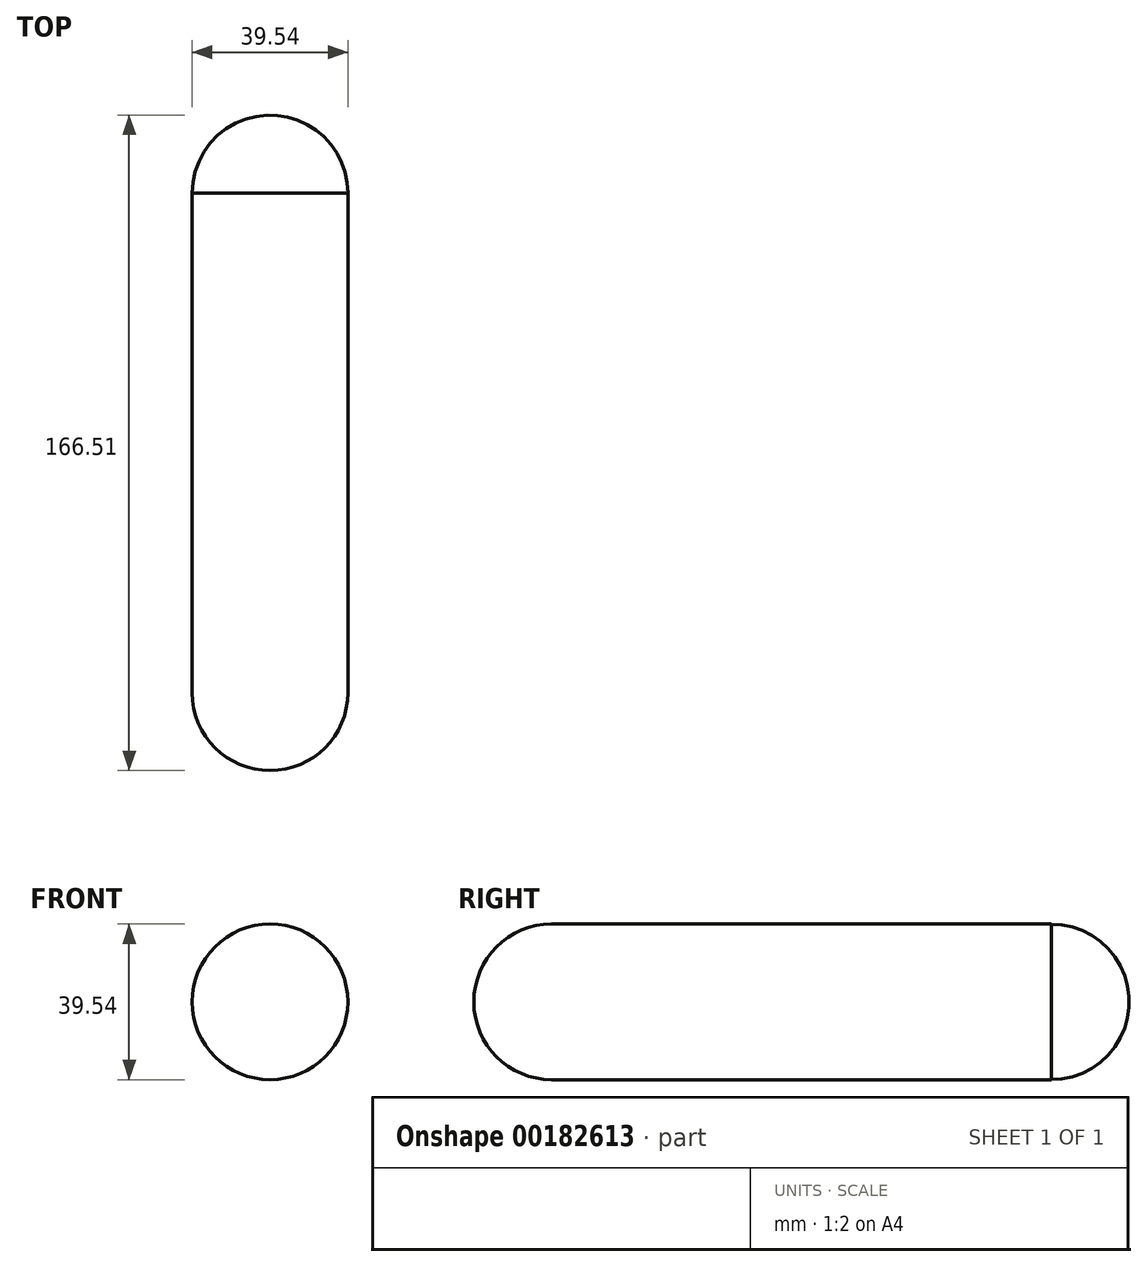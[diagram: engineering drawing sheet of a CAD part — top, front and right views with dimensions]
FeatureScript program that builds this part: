
annotation { "Feature Type Name" : "Feature", "Feature Type Description" : "" }
export const myFeature = defineFeature(function(context is Context, id is Id, definition is map)
    precondition{}
    {
        {
            var Q0;
            Q0=qCreatedBy(makeId("Front.planeOp"),FACE);
            var sketch = newSketch(context, id + "F0", { "sketchPlane" : qUnion([Q0])});
            skCircle(sketch, "E0", {"center": v(0, 0) * mm, "radius": 19.77 * mm});
            skSolve(sketch);
        }
        {
            var Q0;
            Q0=makeQuery(id+"F0.imprint","IMPRINT",FACE,{"disambiguationData":[TD([[makeQuery(id+"F0.imprint","IMPRINT",EDGE,{"derivedFrom":sQuery(id+"F0.wireOp",EDGE,"E0")}),1.0]])]});
            extrude(context, id + "F1", {"entities" : qUnion([Q0]), "endBound" : BoundingType.SYMMETRIC, "depth" : 127 * mm});
        }
        {
            var Q0;
            Q0=makeQuery(id+"F1.opExtrude","CAP_FACE",FACE,{"disambiguationData":[OSD([sQuery(id+"F0.wireOp",EDGE,"E0")])],"isStart":false});
            var sketch = newSketch(context, id + "F2", { "sketchPlane" : qUnion([Q0])});
            skLineSegment(sketch, "E1", {"start": v(-19.77, 0) * mm, "end": v(19.77, 0) * mm});
            skArc(sketch, "E2", {"start": v(19.77, 0) * mm, "mid": v(0, 19.87) * mm, "end": v(-19.77, 0) * mm});
            skSolve(sketch);
        }
        {
            var Q0;
            {var subQ0=sQuery(id+"F2.wireOp",EDGE,"E1");Q0=makeQuery(id+"F2.imprint","IMPRINT",FACE,{"disambiguationData":[TD([[makeQuery(id+"F2.imprint","IMPRINT",EDGE,{"derivedFrom":subQ0}),1.0]])]});}
            var Q1;
            Q1=sQuery(id+"F2.wireOp",EDGE,"E1");
            revolve(context, id + "F3", {"operationType" : NewBodyOperationType.ADD, "entities" : qUnion([Q0]), "axis" : qUnion([Q1]), "revolveType" : RevolveType.ONE_DIRECTION, "angle" : 180 * degree});
        }
        {
            var Q0;
            Q0=makeQuery(id+"F1.opExtrude","CAP_FACE",FACE,{"disambiguationData":[OSD([sQuery(id+"F0.wireOp",EDGE,"E0")])],"isStart":true});
            var sketch = newSketch(context, id + "F4", { "sketchPlane" : qUnion([Q0])});
            skLineSegment(sketch, "E3", {"start": v(-19.77, 0) * mm, "end": v(19.77, 0) * mm});
            skArc(sketch, "E4", {"start": v(19.77, 0) * mm, "mid": v(0, 19.74) * mm, "end": v(-19.77, 0) * mm});
            skSolve(sketch);
        }
        {
            var Q0;
            Q0=makeQuery(id+"F4.imprint","IMPRINT",FACE,{"disambiguationData":[TD([[makeQuery(id+"F4.imprint","IMPRINT",EDGE,{"derivedFrom":sQuery(id+"F4.wireOp",EDGE,"E3")}),1.0]])]});
            var Q1;
            Q1=sQuery(id+"F4.wireOp",EDGE,"E3");
            revolve(context, id + "F5", {"operationType" : NewBodyOperationType.ADD, "entities" : qUnion([Q0]), "axis" : qUnion([Q1]), "revolveType" : RevolveType.ONE_DIRECTION, "angle" : 180 * degree});
        }
    });
